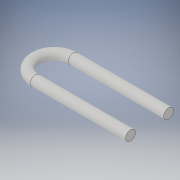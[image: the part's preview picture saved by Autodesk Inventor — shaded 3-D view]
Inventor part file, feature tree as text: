
AUTODESK INVENTOR PART (.ipt)
format: ipt  version: 2019 (Build 230136000, 136)  size: 115,712 bytes
history: native  units: mm
features: sketch x2, sweep x1
ambient origin geometry x8: Origin, YZ Plane, XZ Plane, XY Plane, X Axis, Y Axis, Z Axis, Center Point
bodies: Solid1 (feature_tree)
feature tree (3):
  sweep  "Sweep1"
  sketch  "Sketch1"  dims[d0=5.2mm d1=50.0mm]
  sketch  "Sketch2"  dims[d2=10.0mm d3=180.0deg d4=0.0mm d5=0.0mm]
